FCSTD DOCUMENT  (FreeCAD 1.0R39109 (Git))
Label: male static edge cut
License: All rights reserved
LicenseURL: https://en.wikipedia.org/wiki/All_rights_reserved
objects: Sketcher::SketchObject×1
note: 2 computed .brp shape members not serialized (recipe doc carries the construction recipe); baked Part::Feature solids carry a one-line shape summary decoded from their .brp

FEATURE [Sketcher::SketchObject] Sketch
  ArcFitTolerance = 1e-06
  FullyConstrained = true
  MakeInternals = false
  sketch-geometry (18):
    g0: LineSegment StartX=50 StartY=5 StartZ=0 EndX=50 EndY=85 EndZ=0
    g1: LineSegment StartX=45 StartY=90 StartZ=0 EndX=5 EndY=90 EndZ=0
    g2: LineSegment StartX=0 StartY=85 StartZ=0 EndX=0 EndY=5 EndZ=0
    g3: Circle CenterX=25 CenterY=60 CenterZ=0 NormalX=0 NormalY=0 NormalZ=1 AngleXU=0 Radius=4
    g4: ArcOfCircle CenterX=5 CenterY=85 CenterZ=0 NormalX=0 NormalY=0 NormalZ=1 AngleXU=0 Radius=5 StartAngle=1.5708 EndAngle=3.14159
    g5: GeomPoint X=0 Y=90 Z=0
    g6: ArcOfCircle CenterX=45 CenterY=85 CenterZ=0 NormalX=0 NormalY=0 NormalZ=1 AngleXU=0 Radius=5 StartAngle=1.2e-15 EndAngle=1.5708
    g7: GeomPoint [constr] X=50 Y=90 Z=0
    g8: ArcOfCircle CenterX=5 CenterY=5 CenterZ=0 NormalX=0 NormalY=0 NormalZ=1 AngleXU=0 Radius=5 StartAngle=3.14159 EndAngle=4.71239
    g9: GeomPoint [constr] X=0 Y=0 Z=0
    g10: ArcOfCircle CenterX=45 CenterY=5 CenterZ=0 NormalX=0 NormalY=0 NormalZ=1 AngleXU=0 Radius=5 StartAngle=4.71239 EndAngle=6.28319
    g11: GeomPoint [constr] X=50 Y=0 Z=0
    g12: ArcOfCircle CenterX=25 CenterY=10 CenterZ=0 NormalX=0 NormalY=0 NormalZ=1 AngleXU=0 Radius=4 StartAngle=0 EndAngle=3.14159
    g13: LineSegment [constr] StartX=25 StartY=60 StartZ=0 EndX=25 EndY=10 EndZ=0
    g14: LineSegment StartX=21 StartY=10 StartZ=0 EndX=21 EndY=0 EndZ=0
    g15: LineSegment StartX=29 StartY=10 StartZ=0 EndX=29 EndY=0 EndZ=0
    g16: LineSegment StartX=29 StartY=0 StartZ=0 EndX=45 EndY=0 EndZ=0
    g17: LineSegment StartX=5 StartY=0 StartZ=0 EndX=21 EndY=0 EndZ=0
  constraints (44):
    c: Horizontal(g1)
    c: Vertical(g0)
    c: Vertical(g2)
    c: Coincident(g9,g-1)
    c: DistanceY(g9,g5) = 90
    c: DistanceX(g5,g7) = 50
    c: Diameter(g3) = 8  'radius'
    c: DistanceX(g-1,g3) = 25
    c: Distance(g3,g1) = 30
    c: PointOnObject(g5,g2)
    c: PointOnObject(g5,g1)
    c: Tangent(g2,g4) = -1.5708
    c: Tangent(g1,g4) = -1.5708
    c: PointOnObject(g7,g1)
    c: PointOnObject(g7,g0)
    c: Tangent(g1,g6) = -1.5708
    c: Tangent(g0,g6) = -1.5708
    c: PointOnObject(g9,g2)
    c: Tangent(g2,g8) = -1.5708
    c: PointOnObject(g11,g0)
    c: PointOnObject(g11,g16)
    c: Tangent(g0,g10) = -1.5708
    c: Radius(g4) = 5
    c: Radius(g6) = 5
    c: Radius(g10) = 5
    c: Radius(g8) = 5
    c: Coincident(g13,g3)
    c: Coincident(g13,g12)
    c: Vertical(g13)
    c: Diameter(g12) = 8
    c: Vertical(g14)
    c: PointOnObject(g15,g16)
    c: Vertical(g15)
    c: Tangent(g12,g14) = -1.5708
    c: Tangent(g12,g15) = 1.5708
    c: PointOnObject(g16,g15)
    c: Tangent(g17,g8) = -1.5708
    c: Coincident(g17,g14)
    c: Horizontal(g17)
    c: Horizontal(g16)
    c: PointOnObject(g15,g-1)
    c: DistanceY(g14,g14) = 10
    c: PointOnObject(g14,g-1)
    c: Tangent(g16,g10) = -1.5708
